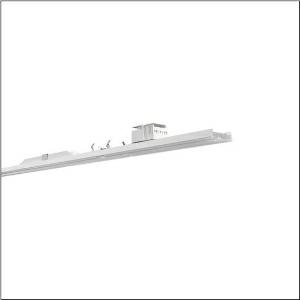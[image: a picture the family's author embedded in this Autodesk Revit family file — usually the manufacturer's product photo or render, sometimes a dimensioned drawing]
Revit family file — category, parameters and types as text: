
# Revit family: licross_r__11_recessed_mo_51tl1edv4e5f_7b7a
name_source: partatom
category: Lighting Fixtures
units: mm (PartAtom-declared; Revit-internal decimal feet)

## family parameters
Cut with Voids When Loaded = No
Host = Face
Light Source = No
Part Type = Normal
Room Calculation Point = No
Round Connector Dimension = Use Diameter
Shared = No

## types (1)
- --- (1 x LED, 14910 lm, 89.6 W, 4000K)
    Apparent Load = 90 VA
    CIE Flux Codes = 85 95 99 100 100
    Color Rendering = 80
    Color Temperature = 4000K
    Default Elevation = 1800 mm
    Description = Licross® 11 Recessed MO, luminaire insert, of sheet steel, galvanised, coil coated, white, length: 2.250mm, width: 66mm, height: 67mm, LED rated luminous flux: 14.910lm, light colour: 840, control gear: DALI 2, control gear: ECG DALI, with plug, 5-pole, with phase selection, mains connection: 220..240V, AC, 50/60Hz, halogen-free wiring, primary optical cover: cover, of PMMA, light emission: direct distribution, protection rating (complete): IP40, insulation class (complete): insulation class I (protective earthing), certification: CE, ENEC, VDE, UKCA, protection symbol: D if used in an environment without relevant dust loads with corresponding accessories, permissible ambient temperature for indoor applications: -25..+35°C, reducing of maximum allowable ambient temperature of 5°C with ceiling mounting, corresponds to IFS (International Featured Standards) requirements for safety and quality in the food industry, LABS conformity tested according to VDMA 24364:2018-05, packaging unit: 1 piece
    Height = 58 mm
    Lamp = 1 x LED
    Lamp Light Flux = 14910 lm
    Lamp Power = 89.6 W
    Lamp count = 1
    Length = 2250 mm
    Luminous efficacy = 166 lm/W
    Manufacturer = Siteco
    ModVariant = No
    Model = 51TL1EDV4E5F
    Mounting Place = Ceiling
    Mounting Type = Pendant
    Number of Poles = 1
    OnlyDefault = Yes
    Power Factor = 1
    Product Name = Licross® 11 Recessed MO
    Product group = luminaire insert
    ProductGroupID = 902
    Protection Class = Protection class I
    Protection Degree = IP 40
    RLX_Detail_Level = 1
    RlxData = <blob elided: 27257 chars, md5=e7b24aa4>
    Socket = socket
    Standby Power = 0 W
    System Light Flux = 14910 lm
    System Power = 90 W
    Type Comments = factory setting: luminous flux: 100 % | dim-lin: 254 | 400 mA
    Type Image = l_1266722.jpg
    URL = http://relux.com
    VarID = @adj_092965
    Voltage = 0 V
    Weight = 0.00 kg
    Width = 66 mm

## geometry (parser evidence)
native form markers: Blend x4, Sweep x10
no freeform markers — native parametric forms only
